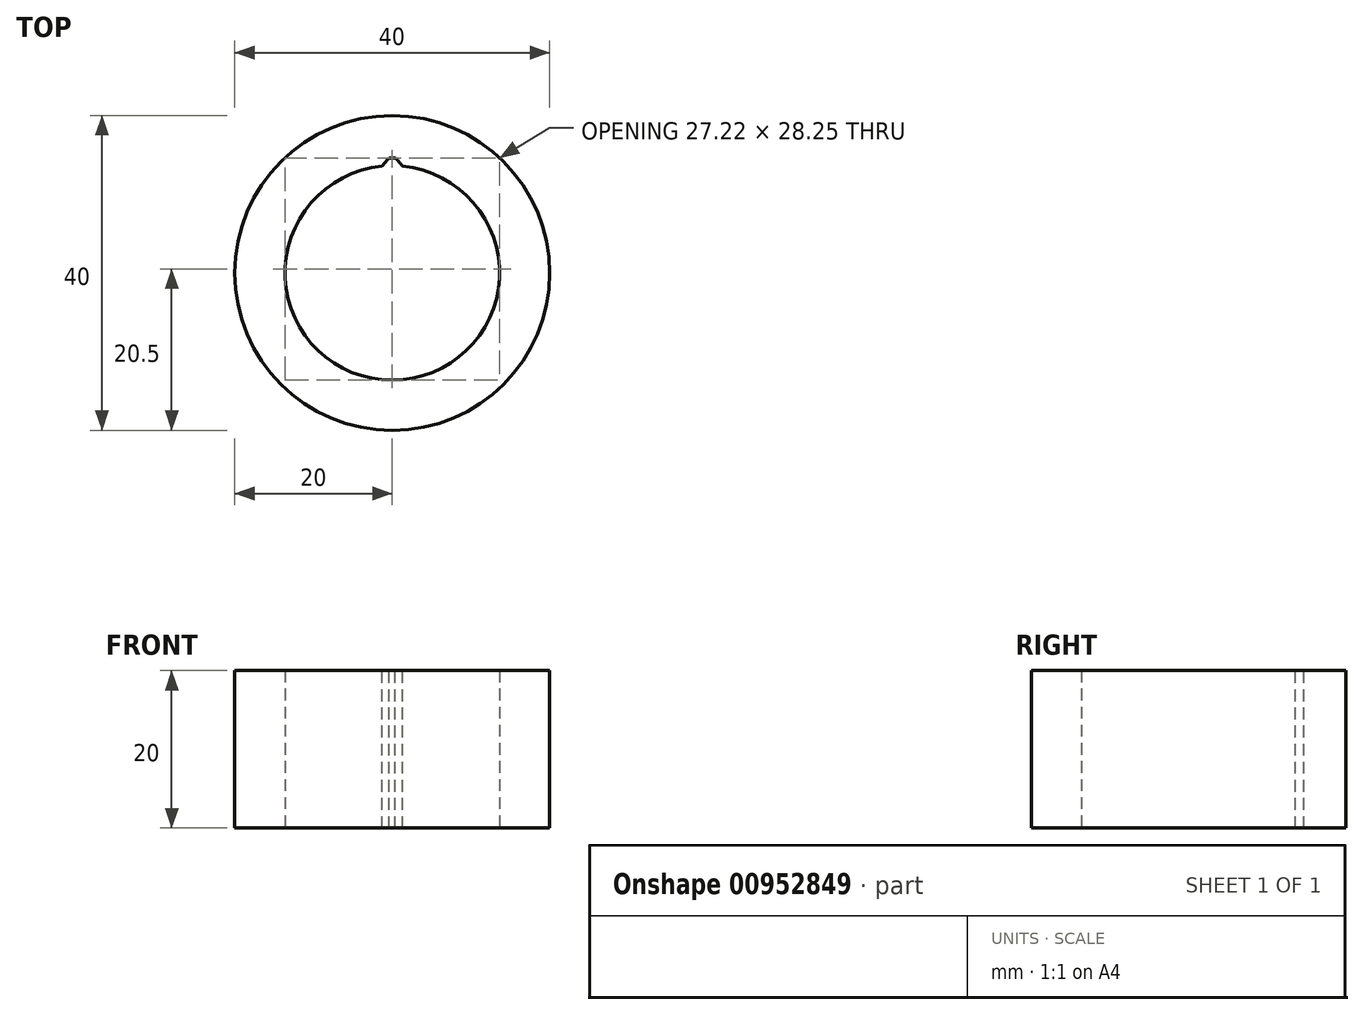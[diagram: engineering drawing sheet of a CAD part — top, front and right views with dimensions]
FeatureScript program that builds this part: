
annotation { "Feature Type Name" : "Feature", "Feature Type Description" : "" }
export const myFeature = defineFeature(function(context is Context, id is Id, definition is map)
    precondition{}
    {
        {
            var Q0;
            Q0=qCreatedBy(makeId("Front.planeOp"),FACE);
            var sketch = newSketch(context, id + "F0", { "sketchPlane" : qUnion([Q0])});
            skLineSegment(sketch, "E0", {"start": v(0, 0) * mm, "end": v(0, 96.08) * mm, "construction": true});
            skLineSegment(sketch, "E1", {"start": v(27, 12) * mm, "end": v(27, 3.23) * mm});
            skLineSegment(sketch, "E2", {"start": v(27, 3.23) * mm, "end": v(28, 1.5) * mm});
            skLineSegment(sketch, "E3", {"start": v(28, 1.5) * mm, "end": v(28, 0) * mm});
            skLineSegment(sketch, "E4", {"start": v(28, 0) * mm, "end": v(62, 0) * mm});
            skLineSegment(sketch, "E5", {"start": v(62, 0) * mm, "end": v(62, -8.5) * mm});
            skLineSegment(sketch, "E6", {"start": v(62, -8.5) * mm, "end": v(32, -8.5) * mm});
            skLineSegment(sketch, "E7", {"start": v(26, -14.5) * mm, "end": v(22, -14.5) * mm});
            skLineSegment(sketch, "E8", {"start": v(20, -16.5) * mm, "end": v(20, -56.5) * mm});
            skArc(sketch, "E9", {"start": v(32, -8.5) * mm, "mid": v(27.76, -10.26) * mm, "end": v(26, -14.5) * mm});
            skLineSegment(sketch, "E10", {"start": v(13.63, -1.73) * mm, "end": v(13.63, -43.9) * mm});
            skLineSegment(sketch, "E11", {"start": v(27, 12) * mm, "end": v(24, 12) * mm});
            skLineSegment(sketch, "E12", {"start": v(24, 12) * mm, "end": v(24, 2) * mm});
            skLineSegment(sketch, "E13", {"start": v(22, 0) * mm, "end": v(14.63, 0) * mm});
            skLineSegment(sketch, "E14", {"start": v(20, -56.5) * mm, "end": v(18, -56.5) * mm});
            skLineSegment(sketch, "E15", {"start": v(18, -56.5) * mm, "end": v(15.13, -51.52) * mm});
            skLineSegment(sketch, "E16", {"start": v(15.13, -51.52) * mm, "end": v(15.13, -46.5) * mm});
            skLineSegment(sketch, "E17", {"start": v(15.13, -46.5) * mm, "end": v(13.63, -43.9) * mm});
            skLineSegment(sketch, "E18", {"start": v(13.63, -1.73) * mm, "end": v(14.63, 0) * mm});
            skPoint(sketch, "E19.visualSharp", {"position": v(24, 0) * mm});
            skArc(sketch, "E19.filletArc", {"start": v(22, 0) * mm, "mid": v(23.41, 0.59) * mm, "end": v(24, 2) * mm});
            skPoint(sketch, "E20.visualSharp", {"position": v(20, -14.5) * mm});
            skArc(sketch, "E20.filletArc", {"start": v(22, -14.5) * mm, "mid": v(20.59, -15.09) * mm, "end": v(20, -16.5) * mm});
            skSolve(sketch);
        }
        {
            var Q0;
            Q0=qSketchRegion(id+"F0",true);
            var Q1;
            Q1=sQuery(id+"F0.wireOp",EDGE,"E0");
            revolve(context, id + "F1", {"surfaceOperationType" : NewSurfaceOperationType.NEW, "entities" : qUnion([Q0]), "axis" : qUnion([Q1]), "revolveType" : RevolveType.FULL});
        }
        {
            var Q0;
            Q0=makeQuery(id+"F1.opRevolve","SWEPT_FACE",FACE,{"disambiguationData":[OSD([sQuery(id+"F0.wireOp",EDGE,"E4")])]});
            var sketch = newSketch(context, id + "F2", { "sketchPlane" : qUnion([Q0])});
            skCircle(sketch, "E21.cCircle", {"center": v(0, 0) * mm, "radius": 57.15 * mm, "construction": true});
            skLineSegment(sketch, "E21.0", {"start": v(0, 57.15) * mm, "end": v(54.35, 17.66) * mm});
            skLineSegment(sketch, "E21.1", {"start": v(54.35, 17.66) * mm, "end": v(33.6, -46.24) * mm});
            skLineSegment(sketch, "E21.2", {"start": v(33.6, -46.24) * mm, "end": v(-33.6, -46.24) * mm});
            skLineSegment(sketch, "E21.3", {"start": v(-33.6, -46.24) * mm, "end": v(-54.35, 17.66) * mm});
            skLineSegment(sketch, "E21.4", {"start": v(-54.35, 17.66) * mm, "end": v(0, 57.15) * mm});
            skSolve(sketch);
        }
        {
            var Q0;
            Q0=makeQuery(id+"F2.imprint","IMPRINT",FACE,{"disambiguationData":[TD([[makeQuery(id+"F2.imprint","IMPRINT",EDGE,{"derivedFrom":sQuery(id+"F2.wireOp",EDGE,"E21.0")}),1.0]])]});
            var sketch = newSketch(context, id + "F3", { "sketchPlane" : qUnion([Q0])});
            skCircle(sketch, "E22.cCircle", {"center": v(0, 0) * mm, "radius": 50 * mm, "construction": true});
            skLineSegment(sketch, "E22.0", {"start": v(0, 50) * mm, "end": v(50, 0) * mm});
            skLineSegment(sketch, "E22.1", {"start": v(50, 0) * mm, "end": v(0, -50) * mm});
            skLineSegment(sketch, "E22.2", {"start": v(0, -50) * mm, "end": v(-50, 0) * mm});
            skLineSegment(sketch, "E22.3", {"start": v(-50, 0) * mm, "end": v(0, 50) * mm});
            skSolve(sketch);
        }
        {
            var Q0;
            Q0=sQuery(id+"F3.wireOp",VERTEX,"E22.0.start");
            var Q1;
            Q1=sQuery(id+"F3.wireOp",VERTEX,"E22.0.end");
            var Q2;
            Q2=sQuery(id+"F3.wireOp",VERTEX,"E22.2.end");
            var Q3;
            Q3=sQuery(id+"F3.wireOp",VERTEX,"E22.1.end");
            var Q4;
            Q4=makeQuery(id+"F1.opRevolve","SWEPT_BODY",BODY,{"disambiguationData":[OSD([sQuery(id+"F0.wireOp",EDGE,"E1"),sQuery(id+"F0.wireOp",EDGE,"E2"),sQuery(id+"F0.wireOp",EDGE,"E3"),sQuery(id+"F0.wireOp",EDGE,"E4"),sQuery(id+"F0.wireOp",EDGE,"E5"),sQuery(id+"F0.wireOp",EDGE,"E6"),sQuery(id+"F0.wireOp",EDGE,"E7"),sQuery(id+"F0.wireOp",EDGE,"E8"),sQuery(id+"F0.wireOp",EDGE,"E9"),sQuery(id+"F0.wireOp",EDGE,"E10"),sQuery(id+"F0.wireOp",EDGE,"E11"),sQuery(id+"F0.wireOp",EDGE,"E12"),sQuery(id+"F0.wireOp",EDGE,"E13"),sQuery(id+"F0.wireOp",EDGE,"E14"),sQuery(id+"F0.wireOp",EDGE,"E15"),sQuery(id+"F0.wireOp",EDGE,"E16"),sQuery(id+"F0.wireOp",EDGE,"E17"),sQuery(id+"F0.wireOp",EDGE,"E18")])]});
            hole(context, id + "F4", {"style" : HoleStyle.SIMPLE, "endStyle" : HoleEndStyle.THROUGH, "standardTappedOrClearance" : lookupTablePath({ "standard" : "ISO", "size" : "14", "type" : "Drilled" }), "standardBlindInLast" : lookupTablePath({ "standard" : "ISO", "size" : "14", "type" : "Drilled" }), "holeDiameter" : 14 * mm, "majorDiameter" : 6.35 * mm, "isTappedThrough" : true, "tappedDepth" : 12.7 * mm, "tapClearance" : 3, "startFromSketch" : true, "locations" : qUnion([Q0, Q1, Q2, Q3]), "scope" : qUnion([Q4])});
        }
        {
            var Q0;
            Q0=makeQuery(id+"F1.opRevolve","SWEPT_FACE",FACE,{"disambiguationData":[OSD([sQuery(id+"F0.wireOp",EDGE,"E13")])]});
            var sketch = newSketch(context, id + "F5", { "sketchPlane" : qUnion([Q0])});
            skCircle(sketch, "E23", {"center": v(0, 0) * mm, "radius": 13.62 * mm});
            skCircle(sketch, "E24", {"center": v(0, 0) * mm, "radius": 14.62 * mm});
            skCircle(sketch, "E25", {"center": v(0, 0) * mm, "radius": 14.2 * mm, "construction": true});
            skLineSegment(sketch, "E26", {"start": v(0, 0) * mm, "end": v(0.8, 14.18) * mm, "construction": true});
            skLineSegment(sketch, "E27", {"start": v(0.8, 14.18) * mm, "end": v(-13.39, 14.97) * mm, "construction": true});
            skLineSegment(sketch, "E28", {"start": v(0.8, 14.18) * mm, "end": v(-6.7, 7.49) * mm, "construction": true});
            skLineSegment(sketch, "E29", {"start": v(-6.7, 7.49) * mm, "end": v(0, 0) * mm, "construction": true});
            skLineSegment(sketch, "E30", {"start": v(0, 0) * mm, "end": v(0, 20.3) * mm, "construction": true});
            skArc(sketch, "E31", {"start": v(-8.04, 6.02) * mm, "mid": v(-7.4, 6.78) * mm, "end": v(-6.7, 7.49) * mm, "construction": true});
            skLineSegment(sketch, "E32", {"start": v(0, 0) * mm, "end": v(-8.04, 6.02) * mm, "construction": true});
            skLineSegment(sketch, "E33", {"start": v(-8.04, 6.02) * mm, "end": v(-0.83, 15.66) * mm, "construction": true});
            skArc(sketch, "E34", {"start": v(-6.7, 7.49) * mm, "mid": v(7.06, -7.14) * mm, "end": v(-7.4, 6.78) * mm, "construction": true});
            skLineSegment(sketch, "E35", {"start": v(0, 0) * mm, "end": v(-7.4, 6.78) * mm, "construction": true});
            skLineSegment(sketch, "E36", {"start": v(-7.4, 6.78) * mm, "end": v(0.06, 14.92) * mm, "construction": true});
            skLineSegment(sketch, "E37", {"start": v(0, 0) * mm, "end": v(1.98, 17.6) * mm, "construction": true});
            skArc(sketch, "E38", {"start": v(-6.7, 7.49) * mm, "mid": v(-7.06, 7.14) * mm, "end": v(-7.4, 6.78) * mm});
            skArc(sketch, "E39", {"start": v(-5.5, 8.4) * mm, "mid": v(-6.11, 7.97) * mm, "end": v(-6.7, 7.49) * mm});
            skLineSegment(sketch, "E40", {"start": v(0, 0) * mm, "end": v(-5.5, 8.4) * mm});
            skLineSegment(sketch, "E41", {"start": v(-5.5, 8.4) * mm, "end": v(1.64, 13.08) * mm});
            skFitSpline(sketch, "E42", {"points": [v(-0.83, 15.66) * mm, v(0.06, 14.92) * mm, v(0.8, 14.18) * mm, v(1.64, 13.08) * mm], "startDerivative": vector(2.8, -2.24) * mm, "endDerivative": vector(2.37, -3.23) * mm});
            skFitSpline(sketch, "E43.MirrorCS", {"points": [v(0.83, 15.66) * mm, v(-0.06, 14.92) * mm, v(-0.8, 14.18) * mm, v(-1.64, 13.08) * mm], "startDerivative": vector(-2.8, -2.24) * mm, "endDerivative": vector(-2.37, -3.23) * mm});
            skSolve(sketch);
        }
        {
            var Q0;
            {var subQ0=sQuery(id+"F5.wireOp",EDGE,"E42");var subQ1=sQuery(id+"F5.wireOp",EDGE,"E23");var subQ2=makeQuery(id+"F5.imprint","INTERSECT",VERTEX,{"derivedFrom":[subQ1,subQ0]});Q0=makeQuery(id+"F5.imprint","IMPRINT",FACE,{"disambiguationData":[TD([[makeQuery(id+"F5.imprint","IMPRINT",EDGE,{"disambiguationData":[TD([[subQ2,-1.0]])],"derivedFrom":subQ1}),-1.0]])]});}
            extrude(context, id + "F6", {"entities" : qUnion([Q0]), "operationType" : NewBodyOperationType.REMOVE, "endBound" : BoundingType.THROUGH_ALL, "oppositeDirection" : true, "depth" : 25 * mm, "offsetDistance" : 25 * mm});
        }
        {
            var Q0;
            Q0=qCreatedBy(makeId("Front.planeOp"),FACE);
            var sketch = newSketch(context, id + "F7", { "sketchPlane" : qUnion([Q0])});
            skLineSegment(sketch, "E44.bottom", {"start": v(-162.98, -16.5) * mm, "end": v(159.3, -16.5) * mm});
            skLineSegment(sketch, "E44.top", {"start": v(-162.98, -36.5) * mm, "end": v(159.3, -36.5) * mm});
            skLineSegment(sketch, "E44.left", {"start": v(-162.98, -16.5) * mm, "end": v(-162.98, -36.5) * mm});
            skLineSegment(sketch, "E44.right", {"start": v(159.3, -16.5) * mm, "end": v(159.3, -36.5) * mm});
            skSolve(sketch);
        }
        {
            var Q0;
            Q0=makeQuery(id+"F7.imprint","IMPRINT",FACE,{"disambiguationData":[TD([[makeQuery(id+"F7.imprint","IMPRINT",EDGE,{"derivedFrom":sQuery(id+"F7.wireOp",EDGE,"E44.bottom")}),-1.0]])]});
            extrude(context, id + "F8", {"entities" : qUnion([Q0]), "depth" : 25 * mm, "offsetDistance" : 25 * mm, "hasSecondDirection" : true, "secondDirectionOppositeDirection" : true, "secondDirectionDepth" : 25 * mm});
        }
        {
            var Q0;
            Q0=makeQuery(id+"F8.opExtrude","SWEPT_BODY",BODY,{"disambiguationData":[OSD([sQuery(id+"F7.wireOp",EDGE,"E44.bottom"),sQuery(id+"F7.wireOp",EDGE,"E44.top"),sQuery(id+"F7.wireOp",EDGE,"E44.left"),sQuery(id+"F7.wireOp",EDGE,"E44.right")])]});
            var Q1;
            Q1=makeQuery(id+"F1.opRevolve","SWEPT_BODY",BODY,{"disambiguationData":[OSD([sQuery(id+"F0.wireOp",EDGE,"E1"),sQuery(id+"F0.wireOp",EDGE,"E2"),sQuery(id+"F0.wireOp",EDGE,"E3"),sQuery(id+"F0.wireOp",EDGE,"E4"),sQuery(id+"F0.wireOp",EDGE,"E5"),sQuery(id+"F0.wireOp",EDGE,"E6"),sQuery(id+"F0.wireOp",EDGE,"E7"),sQuery(id+"F0.wireOp",EDGE,"E8"),sQuery(id+"F0.wireOp",EDGE,"E9"),sQuery(id+"F0.wireOp",EDGE,"E10"),sQuery(id+"F0.wireOp",EDGE,"E11"),sQuery(id+"F0.wireOp",EDGE,"E12"),sQuery(id+"F0.wireOp",EDGE,"E13"),sQuery(id+"F0.wireOp",EDGE,"E14"),sQuery(id+"F0.wireOp",EDGE,"E15"),sQuery(id+"F0.wireOp",EDGE,"E16"),sQuery(id+"F0.wireOp",EDGE,"E17"),sQuery(id+"F0.wireOp",EDGE,"E18"),sQuery(id+"F0.wireOp",EDGE,"E19.filletArc"),sQuery(id+"F0.wireOp",EDGE,"E20.filletArc")])]});
            booleanBodies(context, id + "F9", {"operationType" : BooleanOperationType.INTERSECTION, "tools" : qUnion([Q0, Q1])});
        }
    });
